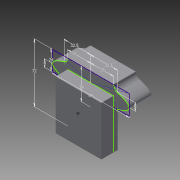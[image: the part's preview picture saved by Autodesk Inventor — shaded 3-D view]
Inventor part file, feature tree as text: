
AUTODESK INVENTOR PART (.ipt)
format: ipt  version: 2013 (Build 170138000, 138)  size: 256,512 bytes
history: native  units: mm
features: sketch x3, extrude x3, fillet x3, hole x1
ambient origin geometry x8: Origin, YZ Plane, XZ Plane, XY Plane, X Axis, Y Axis, Z Axis, Center Point
bodies: Solid1 (feature_tree)
feature tree (10):
  sketch  "Sketch1"  dims[d0=94.0mm d1=24.0mm]
  extrude  "Extrusion3"  Depth=24.0mm
  extrude  "Extrusion4"  Depth=28.0mm
  extrude  "Extrusion5"  Depth=9.0mm
  hole  "Hole1"  [1 undecoded]
  fillet  "Fillet2"  Radius=32.5mm
  fillet  "Fillet3"  Radius=10.0mm
  fillet  "Fillet4"  Radius=72.0mm
  sketch  "Sketch2"  dims[d2=9.0mm d3=28.0mm]
  sketch  "Sketch3"  dims[d4=28.0mm d5=9.0mm d6=32.5mm d7=32.5mm d8=10.0mm d12=72.0mm d16=28.0mm d17=0.0mm d18=15.0mm d19=0.0mm d20=23.0mm d21=0.0mm d22=38.0mm d23=4.978mm d24=10.0mm d25=4.0mm d26=2.0mm d27=90.0deg d28=8.0mm d29=20.594885mm d30=38.0mm d31=1.0mm d32=1.0mm d33=1.0mm]
note: 1 required parameter value undecoded (feature->parameter linkage not recoverable at this tier; creation-order binding heuristic only, values carry confidence <= 0.55)
